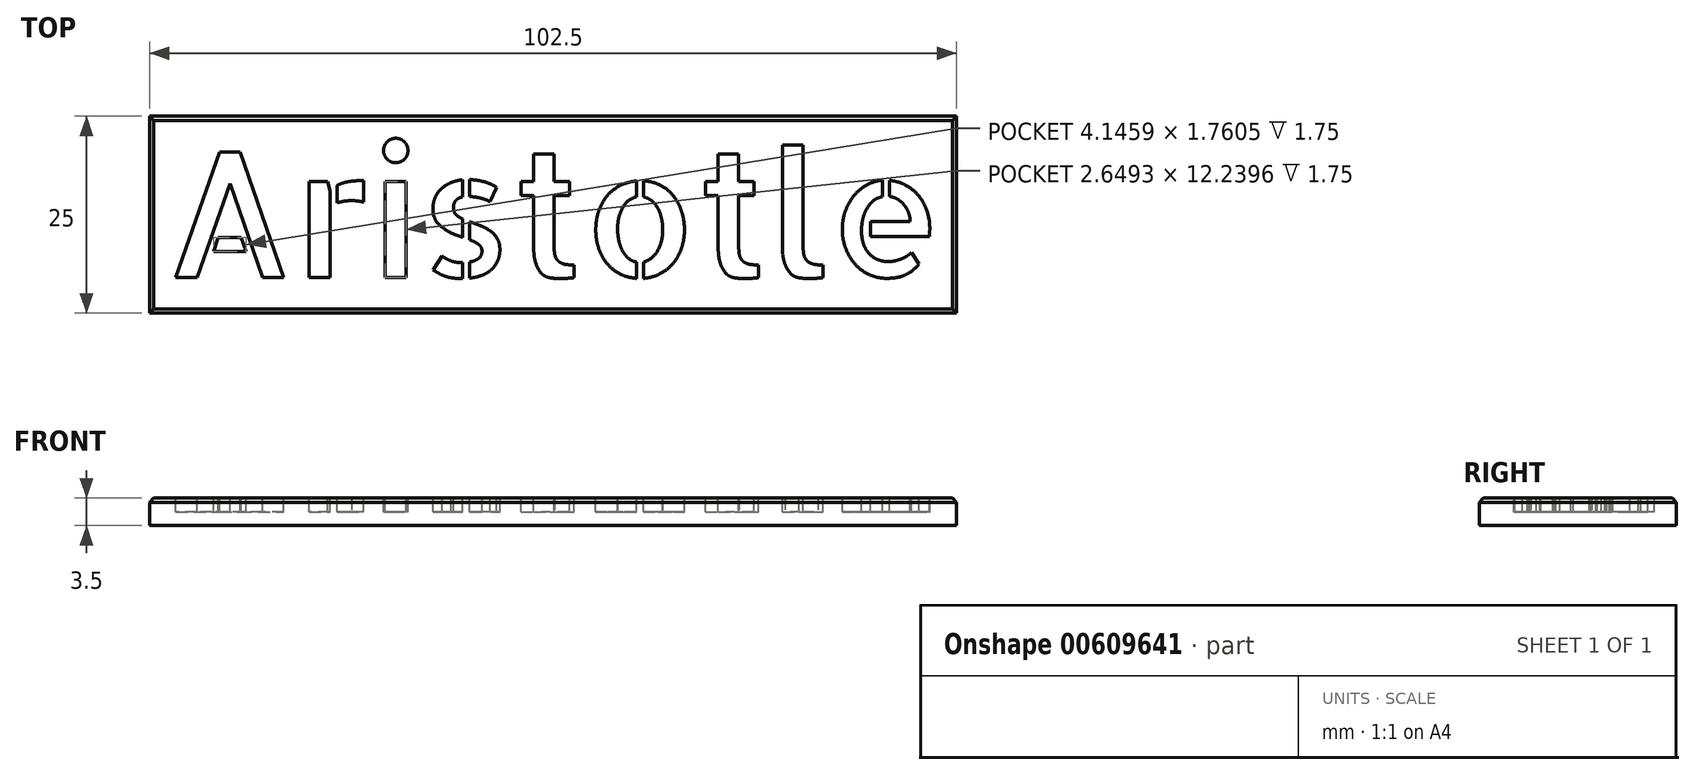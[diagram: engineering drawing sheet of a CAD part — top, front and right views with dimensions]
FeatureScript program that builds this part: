
annotation { "Feature Type Name" : "Feature", "Feature Type Description" : "" }
export const myFeature = defineFeature(function(context is Context, id is Id, definition is map)
    precondition{}
    {
        {
            var Q0;
            Q0=qCreatedBy(makeId("Top.planeOp"),FACE);
            var sketch = newSketch(context, id + "F0", { "sketchPlane" : qUnion([Q0])});
            skLineSegment(sketch, "E0.bottom", {"start": v(-55.03, -1.34) * mm, "end": v(47.47, -1.34) * mm});
            skLineSegment(sketch, "E0.top", {"start": v(-55.03, -26.34) * mm, "end": v(47.47, -26.34) * mm});
            skLineSegment(sketch, "E0.left", {"start": v(-55.03, -1.34) * mm, "end": v(-55.03, -26.34) * mm});
            skLineSegment(sketch, "E0.right", {"start": v(47.47, -1.34) * mm, "end": v(47.47, -26.34) * mm});
            skSolve(sketch);
        }
        {
            var Q0;
            Q0 = qSketchRegion(id + "F0", true);
            extrude(context, id + "F1", {"entities" : qUnion([Q0]), "depth" : 3.5 * mm, "offsetDistance" : 25 * mm});
        }
        {
            var Q0;
            Q0=makeQuery(id+"F1.opExtrude","CAP_FACE",FACE,{"disambiguationData":[OSD([sQuery(id+"F0.wireOp",EDGE,"E0.bottom"),sQuery(id+"F0.wireOp",EDGE,"E0.top"),sQuery(id+"F0.wireOp",EDGE,"E0.left"),sQuery(id+"F0.wireOp",EDGE,"E0.right")])],"isStart":false});
            var sketch = newSketch(context, id + "F2", { "sketchPlane" : qUnion([Q0])});
            skLineSegment(sketch, "E1.0", {"start": v(-55.03, -1.34) * mm, "end": v(-55.03, -26.34) * mm});
            skLineSegment(sketch, "E1.1", {"start": v(-55.03, -1.34) * mm, "end": v(47.47, -1.34) * mm});
            skLineSegment(sketch, "E1.2", {"start": v(47.47, -1.34) * mm, "end": v(47.47, -26.34) * mm});
            skText(sketch, "E2", { "text": "Aristotle", "fontName": "AllertaStencil-Regular.ttf"});
            const initialGuessF2  = {"E2": [-0.05308, -0.02184, 1, 0, 0.016]};
            skSetInitialGuess(sketch, initialGuessF2);
            skSolve(sketch);
        }
        {
            var Q0;
            Q0 = qSketchRegion(id + "F2", true);
            extrude(context, id + "F3", {"entities" : qUnion([Q0]), "operationType" : NewBodyOperationType.REMOVE, "oppositeDirection" : true, "depth" : 1.75 * mm, "offsetDistance" : 25 * mm});
        }
        {
            var Q0;
            Q0=makeQuery(id+"F1.opExtrude","CAP_EDGE",EDGE,{"disambiguationData":[OSD([sQuery(id+"F0.wireOp",EDGE,"E0.right")])],"isStart":false});
            var Q1;
            Q1=makeQuery(id+"F1.opExtrude","CAP_EDGE",EDGE,{"disambiguationData":[OSD([sQuery(id+"F0.wireOp",EDGE,"E0.bottom")])],"isStart":false});
            var Q2;
            Q2=makeQuery(id+"F1.opExtrude","CAP_EDGE",EDGE,{"disambiguationData":[OSD([sQuery(id+"F0.wireOp",EDGE,"E0.top")])],"isStart":false});
            var Q3;
            Q3=makeQuery(id+"F1.opExtrude","CAP_EDGE",EDGE,{"disambiguationData":[OSD([sQuery(id+"F0.wireOp",EDGE,"E0.left")])],"isStart":false});
            chamfer(context, id + "F4", {"entities" : qUnion([Q0, Q1, Q2, Q3]), "width" : .525 * mm, "tangentPropagation" : true});
        }
    });
